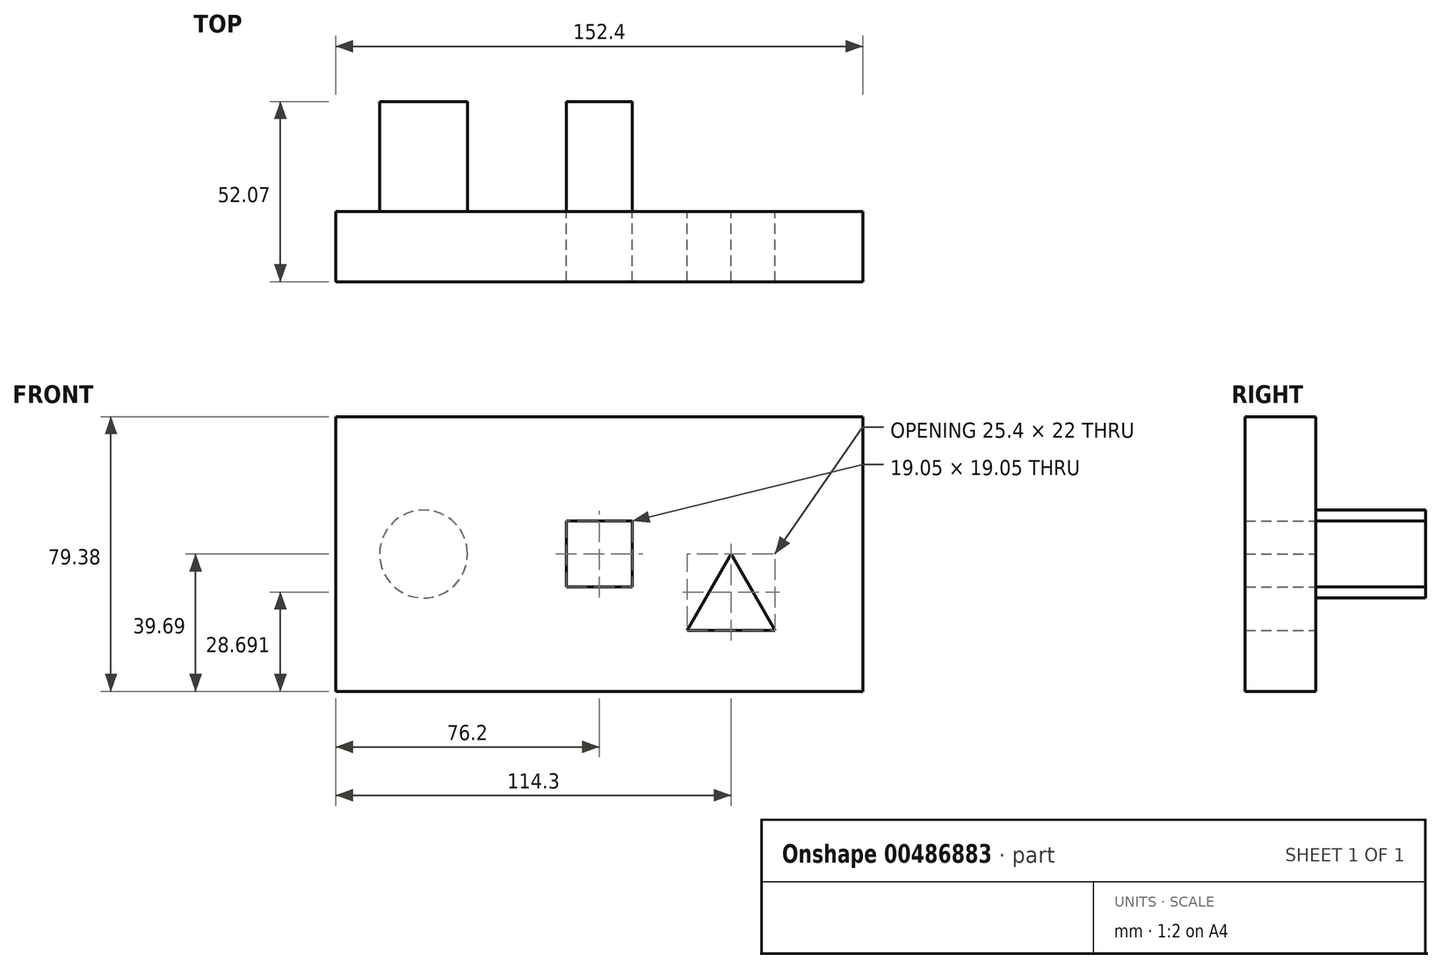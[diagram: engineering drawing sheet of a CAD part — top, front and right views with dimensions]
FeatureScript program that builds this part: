
annotation { "Feature Type Name" : "Feature", "Feature Type Description" : "" }
export const myFeature = defineFeature(function(context is Context, id is Id, definition is map)
    precondition{}
    {
        {
            var Q0;
            Q0=qCreatedBy(makeId("Front.planeOp"),FACE);
            var sketch = newSketch(context, id + "F0", { "sketchPlane" : qUnion([Q0])});
            skLineSegment(sketch, "E0", {"start": v(0, 0) * mm, "end": v(-31.75, 0) * mm});
            skLineSegment(sketch, "E1.bottom", {"start": v(-107.95, 39.69) * mm, "end": v(44.45, 39.69) * mm});
            skLineSegment(sketch, "E1.top", {"start": v(-107.95, -39.69) * mm, "end": v(44.45, -39.69) * mm});
            skLineSegment(sketch, "E1.left", {"start": v(-107.95, 39.69) * mm, "end": v(-107.95, -39.69) * mm});
            skLineSegment(sketch, "E1.right", {"start": v(44.45, 39.69) * mm, "end": v(44.45, -39.69) * mm});
            skPoint(sketch, "E1.middle", {"position": v(-31.75, 0) * mm});
            skLineSegment(sketch, "E2.bottom", {"start": v(-41.27, 9.53) * mm, "end": v(-22.22, 9.53) * mm});
            skLineSegment(sketch, "E2.top", {"start": v(-41.27, -9.53) * mm, "end": v(-22.22, -9.53) * mm});
            skLineSegment(sketch, "E2.left", {"start": v(-41.27, 9.52) * mm, "end": v(-41.27, -9.53) * mm});
            skLineSegment(sketch, "E2.right", {"start": v(-22.22, 9.53) * mm, "end": v(-22.22, -9.53) * mm});
            skLineSegment(sketch, "E3", {"start": v(-31.75, 0) * mm, "end": v(-82.55, 0) * mm});
            skCircle(sketch, "E4", {"center": v(-82.55, 0) * mm, "radius": 12.7 * mm});
            skLineSegment(sketch, "E5", {"start": v(0, 0) * mm, "end": v(6.35, 0) * mm});
            skLineSegment(sketch, "E6", {"start": v(-6.35, -22) * mm, "end": v(6.35, 0) * mm});
            skLineSegment(sketch, "E7", {"start": v(6.35, 0) * mm, "end": v(19.05, -22) * mm});
            skLineSegment(sketch, "E8", {"start": v(19.05, -22) * mm, "end": v(-6.35, -22) * mm});
            skSolve(sketch);
        }
        {
            var Q0;
            Q0=makeQuery(id+"F0.imprint","IMPRINT",FACE,{"disambiguationData":[TD([[makeQuery(id+"F0.imprint","IMPRINT",EDGE,{"derivedFrom":sQuery(id+"F0.wireOp",EDGE,"E1.bottom")}),-1.0]])]});
            var Q1;
            Q1=makeQuery(id+"F0.imprint","IMPRINT",FACE,{"disambiguationData":[TD([[makeQuery(id+"F0.imprint","IMPRINT",EDGE,{"derivedFrom":sQuery(id+"F0.wireOp",EDGE,"E4")}),1.0]])]});
            var Q2;
            {var subQ1=sQuery(id+"F0.wireOp",EDGE,"E2.bottom");Q2=makeQuery(id+"F0.imprint","IMPRINT",FACE,{"disambiguationData":[TD([[makeQuery(id+"F0.imprint","IMPRINT",EDGE,{"derivedFrom":subQ1}),-1.0]])]});}
            var Q3;
            {var subQ1=sQuery(id+"F0.wireOp",EDGE,"E2.top");Q3=makeQuery(id+"F0.imprint","IMPRINT",FACE,{"disambiguationData":[TD([[makeQuery(id+"F0.imprint","IMPRINT",EDGE,{"derivedFrom":subQ1}),1.0]])]});}
            var Q4;
            Q4=makeQuery(id+"F0.imprint","IMPRINT",FACE,{"disambiguationData":[TD([[makeQuery(id+"F0.imprint","IMPRINT",EDGE,{"derivedFrom":sQuery(id+"F0.wireOp",EDGE,"E6")}),-1.0]])]});
            extrude(context, id + "F1", {"entities" : qUnion([Q0, Q1, Q2, Q3, Q4]), "depth" : 20.32 * mm});
        }
        {
            var Q0;
            Q0=makeQuery(id+"F0.imprint","IMPRINT",FACE,{"disambiguationData":[TD([[makeQuery(id+"F0.imprint","IMPRINT",EDGE,{"derivedFrom":sQuery(id+"F0.wireOp",EDGE,"E4")}),1.0]])]});
            extrude(context, id + "F2", {"entities" : qUnion([Q0]), "operationType" : NewBodyOperationType.ADD, "oppositeDirection" : true, "depth" : 31.75 * mm});
        }
        {
            var Q0;
            {var subQ1=sQuery(id+"F0.wireOp",EDGE,"E2.bottom");Q0=makeQuery(id+"F0.imprint","IMPRINT",FACE,{"disambiguationData":[TD([[makeQuery(id+"F0.imprint","IMPRINT",EDGE,{"derivedFrom":subQ1}),-1.0]])]});}
            var Q1;
            {var subQ1=sQuery(id+"F0.wireOp",EDGE,"E2.top");Q1=makeQuery(id+"F0.imprint","IMPRINT",FACE,{"disambiguationData":[TD([[makeQuery(id+"F0.imprint","IMPRINT",EDGE,{"derivedFrom":subQ1}),1.0]])]});}
            extrude(context, id + "F3", {"entities" : qUnion([Q0, Q1]), "operationType" : NewBodyOperationType.ADD, "oppositeDirection" : true, "depth" : 31.75 * mm});
        }
        {
            var Q0;
            {var subQ1=sQuery(id+"F0.wireOp",EDGE,"E2.bottom");Q0=makeQuery(id+"F0.imprint","IMPRINT",FACE,{"disambiguationData":[TD([[makeQuery(id+"F0.imprint","IMPRINT",EDGE,{"derivedFrom":subQ1}),-1.0]])]});}
            var Q1;
            {var subQ1=sQuery(id+"F0.wireOp",EDGE,"E2.top");Q1=makeQuery(id+"F0.imprint","IMPRINT",FACE,{"disambiguationData":[TD([[makeQuery(id+"F0.imprint","IMPRINT",EDGE,{"derivedFrom":subQ1}),1.0]])]});}
            extrude(context, id + "F4", {"entities" : qUnion([Q0, Q1]), "operationType" : NewBodyOperationType.REMOVE, "oppositeDirection" : true, "depth" : -20.32 * mm});
        }
        {
            var Q0;
            Q0=makeQuery(id+"F0.imprint","IMPRINT",FACE,{"disambiguationData":[TD([[makeQuery(id+"F0.imprint","IMPRINT",EDGE,{"derivedFrom":sQuery(id+"F0.wireOp",EDGE,"E6")}),-1.0]])]});
            extrude(context, id + "F5", {"entities" : qUnion([Q0]), "operationType" : NewBodyOperationType.REMOVE, "depth" : 25.4 * mm});
        }
    });
